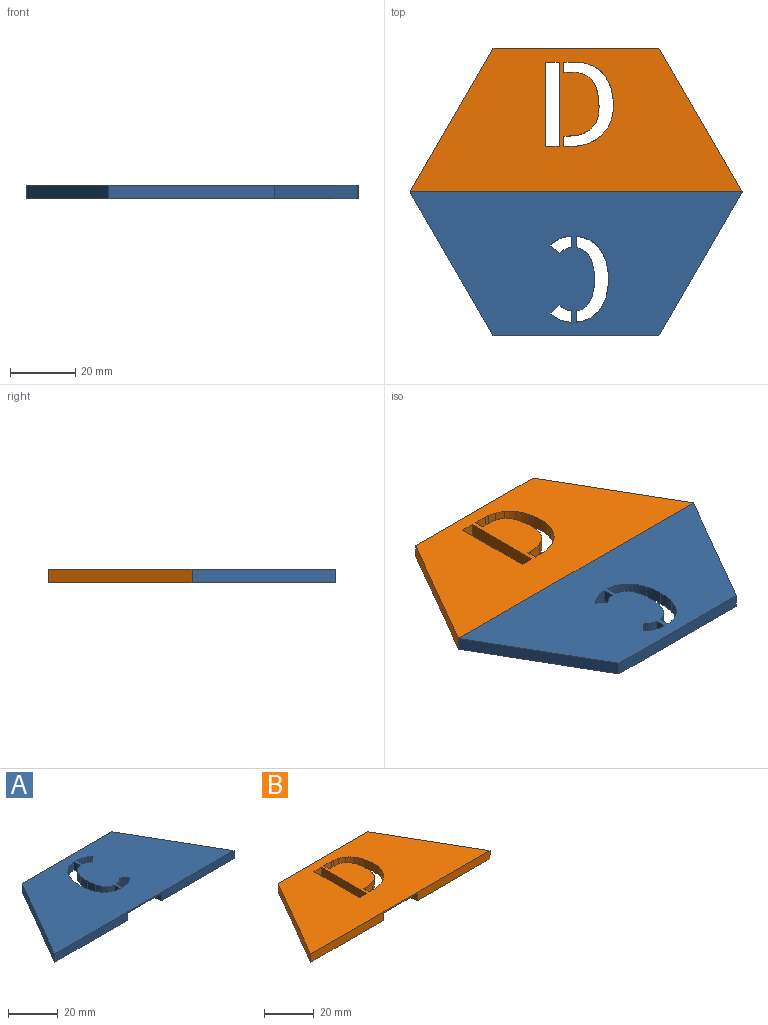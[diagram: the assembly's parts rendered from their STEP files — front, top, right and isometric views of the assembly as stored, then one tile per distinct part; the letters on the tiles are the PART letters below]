
ASSEMBLY  parts=2 mates=1
PART A: 37 faces, bbox 101.6x44x4 mm
  f0: plane 101.6x43.99mm, normal (0,0,-1), area 3044.2mm2, adj f2,f3,f4,f5,f6,f8,f9,f10
  f1: plane 101.6x43.99mm, normal (0,0,1), area 3189.8mm2, adj f2,f3,f4,f5,f8,f9,f10,f11
  f2: plane 50.8x4mm, normal (0,1,0), area 203.2mm2, adj f0,f1,f3,f4
  f3: plane 43.99x25.4mm, normal (0.87,0.5,0), area 203.2mm2, adj f0,f1,f2,f5
  f4: plane 43.99x25.4mm, normal (-0.87,0.5,0), area 203.2mm2, adj f0,f1,f2,f5
  f5: plane 101.6x4mm, normal (0,-1,0), area 339mm2, adj f0,f1,f3,f4,f6,f7
  f6: cylinder r=9.62mm len=19.25mm, axis (0,0,-1), area 105.8mm2, adj f0,f5,f7
  f7: plane 19.25x9.63mm, normal (0,0,-1), area 145.5mm2, adj f5,f6
  f8: plane 4x3.46mm, normal (1,0,0), area 13.9mm2, adj f0,f1,f9,f13
  f9: extruded ~4x3.6mm, area 14.8mm2, adj f0,f1,f8,f10
  f10: extruded ~4x2.97mm, area 14.4mm2, adj f0,f1,f9,f11
  f11: plane 4x2.9mm, normal (-0.66,0.75,0), area 15.5mm2, adj f0,f1,f10,f12
  f12: extruded ~4x1.7mm, area 8.7mm2, adj f0,f1,f11,f13
  f13: extruded ~4x1.97mm, area 8.3mm2, adj f0,f1,f8,f12
  f14: plane 4x2.9mm, normal (-0.66,-0.75,0), area 15.5mm2, adj f0,f1,f15,f18
  f15: extruded ~6.57x4mm, area 29.2mm2, adj f0,f1,f14,f16
  f16: plane 4x3.46mm, normal (1,0,0), area 13.9mm2, adj f0,f1,f15,f17
  f17: extruded ~4x1.96mm, area 8.2mm2, adj f0,f1,f16,f18
  f18: extruded ~4x1.71mm, area 8.8mm2, adj f0,f1,f14,f17
  f19: extruded ~5.5x4mm, area 22.3mm2, adj f0,f1,f20,f36
  f20: extruded ~4.04x4mm, area 18.3mm2, adj f0,f1,f19,f21
  f21: extruded ~4x3.13mm, area 16.3mm2, adj f0,f1,f20,f22
  f22: extruded ~4x3.94mm, area 16.4mm2, adj f0,f1,f21,f23
  f23: plane 4x3.43mm, normal (-1,0,0), area 13.7mm2, adj f0,f1,f22,f24
  f24: extruded ~4x2.15mm, area 9.2mm2, adj f0,f1,f23,f25
  f25: extruded ~4x1.82mm, area 10.3mm2, adj f0,f1,f24,f26
  f26: extruded ~4x2.94mm, area 12.8mm2, adj f0,f1,f25,f27
  f27: extruded ~4.19x4mm, area 16.9mm2, adj f0,f1,f26,f28
  f28: extruded ~4.18x4mm, area 16.9mm2, adj f0,f1,f27,f29
  f29: extruded ~4x2.92mm, area 12.7mm2, adj f0,f1,f28,f30
  f30: extruded ~4x1.78mm, area 10.1mm2, adj f0,f1,f29,f31
  f31: extruded ~4x2.17mm, area 9.3mm2, adj f0,f1,f30,f32
  f32: plane 4x3.5mm, normal (-1,0,0), area 14mm2, adj f0,f1,f31,f33
  f33: extruded ~4x3.94mm, area 16.4mm2, adj f0,f1,f32,f34
  f34: extruded ~4x3.13mm, area 16.3mm2, adj f0,f1,f33,f35
  f35: extruded ~4.02x4mm, area 18.2mm2, adj f0,f1,f34,f36
  f36: extruded ~5.49x4mm, area 22.2mm2, adj f0,f1,f19,f35
PART B: 34 faces, bbox 101.6x44x4 mm
  f0: plane 101.6x43.99mm, normal (0,0,-1), area 2949.1mm2, adj f2,f3,f4,f5,f6,f8,f9,f10
  f1: plane 101.6x43.99mm, normal (0,0,1), area 3094.6mm2, adj f2,f3,f4,f5,f8,f9,f10,f11
  f2: plane 43.99x25.4mm, normal (-0.87,0.5,0), area 203.2mm2, adj f0,f1,f4,f5
  f3: plane 43.99x25.4mm, normal (0.87,0.5,0), area 203.2mm2, adj f0,f1,f4,f5
  f4: plane 50.8x4mm, normal (0,1,0), area 203.2mm2, adj f0,f1,f2,f3
  f5: plane 101.6x4mm, normal (0,-1,0), area 339mm2, adj f0,f1,f2,f3,f6,f7
  f6: cylinder r=9.62mm len=19.25mm, axis (0,0,-1), area 105.8mm2, adj f0,f5,f7
  f7: plane 19.25x9.63mm, normal (0,0,-1), area 145.5mm2, adj f5,f6
  f8: plane 4x2.14mm, normal (0,1,0), area 8.5mm2, adj f0,f1,f9,f29
  f9: plane 4x3.18mm, normal (1,0,0), area 12.7mm2, adj f0,f1,f8,f10
  f10: plane 4x1.02mm, normal (0,-1,0), area 4.1mm2, adj f0,f1,f9,f11
  f11: extruded ~4.89x4mm, area 19.9mm2, adj f0,f1,f10,f12
  f12: extruded ~4x2.99mm, area 14.7mm2, adj f0,f1,f11,f13
  f13: extruded ~4x2.85mm, area 13mm2, adj f0,f1,f12,f14
  f14: extruded ~4x3.18mm, area 12.9mm2, adj f0,f1,f13,f15
  f15: extruded ~7.9x4mm, area 33mm2, adj f0,f1,f14,f16
  f16: extruded ~6.15x4mm, area 28.1mm2, adj f0,f1,f15,f17
  f17: plane 4x2.73mm, normal (0,1,0), area 10.9mm2, adj f0,f1,f16,f18
  f18: plane 4x3.08mm, normal (1,0,0), area 12.3mm2, adj f0,f1,f17,f19
  f19: plane 4.13x4mm, normal (0,-1,0), area 16.5mm2, adj f0,f1,f18,f20
  f20: extruded ~4x1.5mm, area 6mm2, adj f0,f1,f19,f21
  f21: extruded ~4x2.24mm, area 9.2mm2, adj f0,f1,f20,f22
  f22: extruded ~4x2.53mm, area 11.4mm2, adj f0,f1,f21,f23
  f23: extruded ~4x2.39mm, area 13.5mm2, adj f0,f1,f22,f24
  f24: extruded ~4x3.78mm, area 16.7mm2, adj f0,f1,f23,f25
  f25: extruded ~5.43x4mm, area 22mm2, adj f0,f1,f24,f26
  f26: extruded ~4.49x4mm, area 18.4mm2, adj f0,f1,f25,f27
  f27: extruded ~4x3.9mm, area 18.5mm2, adj f0,f1,f26,f28
  f28: extruded ~4.09x4mm, area 19.8mm2, adj f0,f1,f27,f29
  f29: extruded ~5.71x4mm, area 23.4mm2, adj f0,f1,f8,f28
  f30: plane 25.77x4mm, normal (1,0,0), area 103.1mm2, adj f0,f1,f31,f33
  f31: plane 4.2x4mm, normal (0,-1,0), area 16.8mm2, adj f0,f1,f30,f32
  f32: plane 25.77x4mm, normal (-1,0,0), area 103.1mm2, adj f0,f1,f31,f33
  f33: plane 4.2x4mm, normal (0,1,0), area 16.8mm2, adj f0,f1,f30,f32
PLACE A rot(axis=(0,0,1),180deg) t=(0,-87.99,0)mm
PLACE B at identity
MATE planar A.f5 <-> B.f5  axis (0,1,0) through (0,0,2.05)mm
